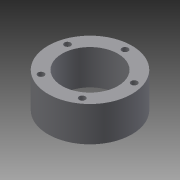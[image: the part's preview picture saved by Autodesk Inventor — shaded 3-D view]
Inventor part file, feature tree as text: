
AUTODESK INVENTOR PART (.ipt)
format: ipt  version: 2014 (Build 180170000, 170)  size: 91,136 bytes
history: native  units: mm
features: extrude x1, sketch x1
ambient origin geometry x8: Origin, YZ Plane, XZ Plane, XY Plane, X Axis, Y Axis, Z Axis, Center Point
bodies: Solid1 (feature_tree)
feature tree (2):
  extrude  "Extrusion1"  Depth=50.0mm
  sketch  "Sketch1"  dims[d0=95.5mm d1=9.0mm d2=80.0mm d3=120.0mm d4=50.0mm d5=0.0mm]
